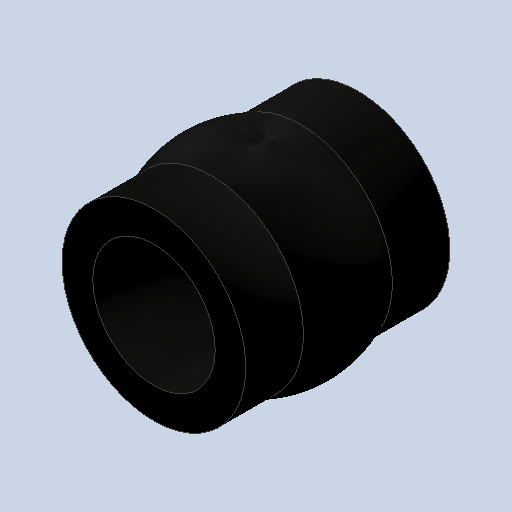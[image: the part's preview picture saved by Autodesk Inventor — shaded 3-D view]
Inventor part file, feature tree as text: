
AUTODESK INVENTOR PART (.ipt)
format: ipt  version: 2023 (Build 270158030, 158C)  size: 138,752 bytes
history: native  units: mm
features: sketch x3, extrude x2, other x1, revolve x1
ambient origin geometry x8: Origin, YZ Plane, XZ Plane, XY Plane, X Axis, Y Axis, Z Axis, Center Point
bodies: Body1 (feature_tree)
feature tree (7):
  other  "ソリッド1"
  revolve  "回転1"
  extrude  "押し出し1"  Depth=2.5mm
  extrude  "押し出し2"  Depth=2.5mm
  sketch  "スケッチ1"
  sketch  "スケッチ2"
  sketch  "スケッチ3"
